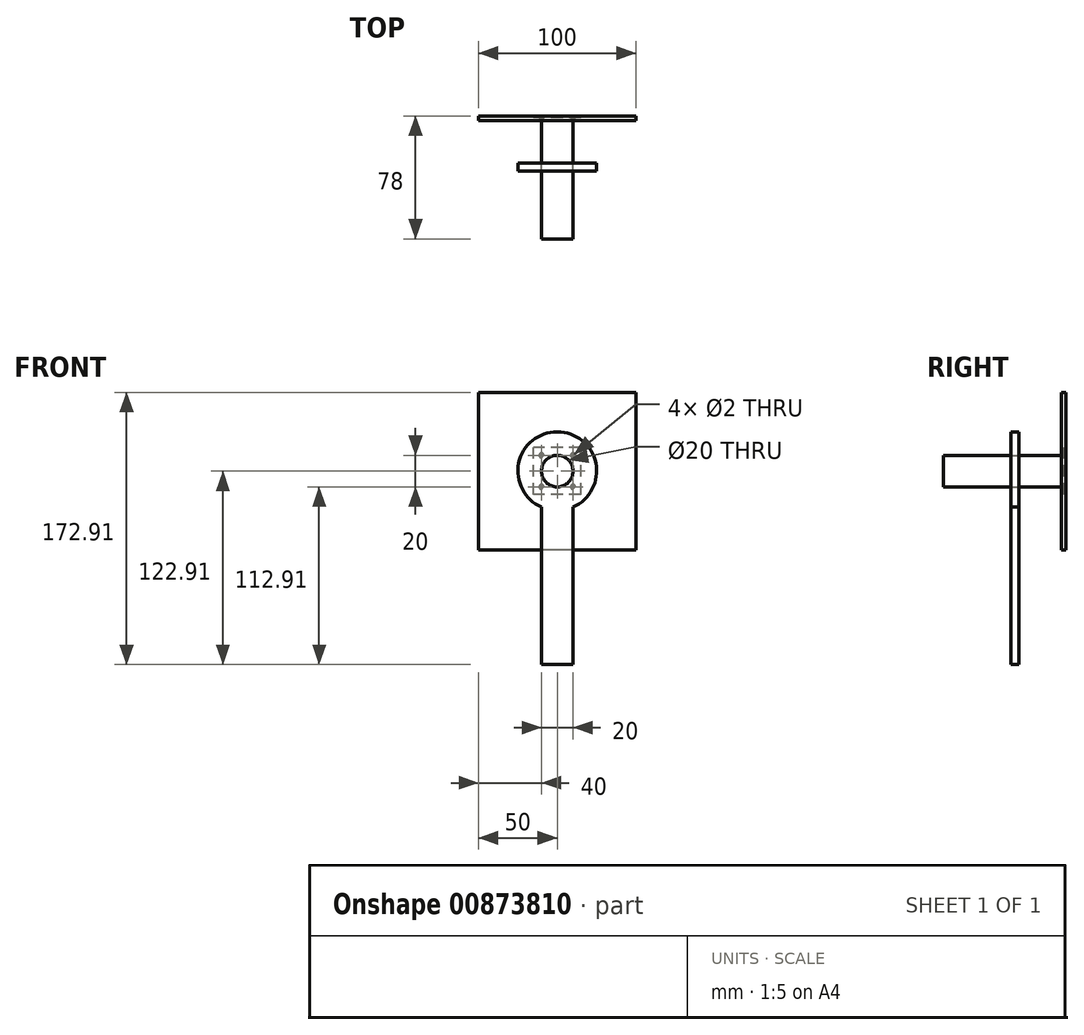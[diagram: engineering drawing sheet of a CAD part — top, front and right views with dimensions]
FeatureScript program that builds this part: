
annotation { "Feature Type Name" : "Feature", "Feature Type Description" : "" }
export const myFeature = defineFeature(function(context is Context, id is Id, definition is map)
    precondition{}
    {
        {
            var Q0;
            Q0=qCreatedBy(makeId("Front.planeOp"),FACE);
            var sketch = newSketch(context, id + "F0", { "sketchPlane" : qUnion([Q0])});
            skArc(sketch, "E0", {"start": v(0, 25) * mm, "mid": v(25, 0) * mm, "end": v(0, -25) * mm});
            skLineSegment(sketch, "E1", {"start": v(0, -25) * mm, "end": v(0, -122.91) * mm});
            skLineSegment(sketch, "E2", {"start": v(0, -122.91) * mm, "end": v(10, -122.91) * mm});
            skLineSegment(sketch, "E3", {"start": v(10, -122.91) * mm, "end": v(10, -22.91) * mm});
            skLineSegment(sketch, "E4", {"start": v(0, 25) * mm, "end": v(0, -25) * mm, "construction": true});
            skArc(sketch, "E5.MirrorCS", {"start": v(0, 25) * mm, "mid": v(-25, 0) * mm, "end": v(0, -25) * mm});
            skLineSegment(sketch, "E6.MirrorCS", {"start": v(-10, -122.91) * mm, "end": v(-10, -22.91) * mm});
            skLineSegment(sketch, "E7", {"start": v(-10, -122.91) * mm, "end": v(0, -122.91) * mm});
            skSolve(sketch);
        }
        {
            var Q0;
            Q0 = qSketchRegion(id + "F0", true);
            extrude(context, id + "F1", {"entities" : qUnion([Q0]), "depth" : 5 * mm, "offsetDistance" : 25 * mm});
        }
        {
            var Q0;
            Q0=qCreatedBy(makeId("Front.planeOp"),FACE);
            var sketch = newSketch(context, id + "F2", { "sketchPlane" : qUnion([Q0])});
            skCircle(sketch, "E8", {"center": v(0, 0) * mm, "radius": 10 * mm});
            skSolve(sketch);
        }
        {
            var Q0;
            Q0 = qSketchRegion(id + "F2", true);
            extrude(context, id + "F3", {"entities" : qUnion([Q0]), "depth" : 75 * mm, "offsetDistance" : 25 * mm});
        }
        {
            var Q0;
            Q0=makeQuery(id+"F3.opExtrude","SWEPT_BODY",BODY,{"disambiguationData":[OSD([sQuery(id+"F2.wireOp",EDGE,"E8")])]});
            var Q1;
            Q1=makeQuery(id+"F1.opExtrude","SWEPT_BODY",BODY,{"disambiguationData":[OSD([sQuery(id+"F0.wireOp",EDGE,"E0"),sQuery(id+"F0.wireOp",EDGE,"E2"),sQuery(id+"F0.wireOp",EDGE,"E3"),sQuery(id+"F0.wireOp",EDGE,"E5.MirrorCS"),sQuery(id+"F0.wireOp",EDGE,"E6.MirrorCS"),sQuery(id+"F0.wireOp",EDGE,"E7")])]});
            booleanBodies(context, id + "F4", {"operationType" : BooleanOperationType.SUBTRACTION, "tools" : qUnion([Q0]), "targets" : qUnion([Q1]), "keepTools" : true});
        }
        {
            var Q0;
            Q0=qCreatedBy(makeId("Front.planeOp"),FACE);
            var sketch = newSketch(context, id + "F5", { "sketchPlane" : qUnion([Q0])});
            skLineSegment(sketch, "E9.bottom", {"start": v(50, -50) * mm, "end": v(-50, -50) * mm});
            skLineSegment(sketch, "E9.top", {"start": v(50, 50) * mm, "end": v(-50, 50) * mm});
            skLineSegment(sketch, "E9.left", {"start": v(50, -50) * mm, "end": v(50, 50) * mm});
            skLineSegment(sketch, "E9.right", {"start": v(-50, -50) * mm, "end": v(-50, 50) * mm});
            skPoint(sketch, "E9.middle", {"position": v(0, 0) * mm});
            skSolve(sketch);
        }
        {
            var Q0;
            Q0 = qSketchRegion(id + "F5", true);
            extrude(context, id + "F6", {"entities" : qUnion([Q0]), "depth" : 3 * mm, "offsetDistance" : 25 * mm});
        }
        {
            var Q0;
            Q0=qCreatedBy(makeId("Front.planeOp"),FACE);
            var sketch = newSketch(context, id + "F7", { "sketchPlane" : qUnion([Q0])});
            skLineSegment(sketch, "E10.bottom", {"start": v(15, -15) * mm, "end": v(-15, -15) * mm});
            skLineSegment(sketch, "E10.top", {"start": v(15, 15) * mm, "end": v(-15, 15) * mm});
            skLineSegment(sketch, "E10.left", {"start": v(15, -15) * mm, "end": v(15, 15) * mm});
            skLineSegment(sketch, "E10.right", {"start": v(-15, -15) * mm, "end": v(-15, 15) * mm});
            skPoint(sketch, "E10.middle", {"position": v(0, 0) * mm});
            skSolve(sketch);
        }
        {
            var Q0;
            Q0 = qSketchRegion(id + "F7", true);
            extrude(context, id + "F8", {"entities" : qUnion([Q0]), "depth" : 1 * mm, "offsetDistance" : 25 * mm});
        }
        {
            var Q0;
            Q0=makeQuery(id+"F3.opExtrude","SWEPT_BODY",BODY,{"disambiguationData":[OSD([sQuery(id+"F2.wireOp",EDGE,"E8")])]});
            transform(context, id + "F9", {"entities" : qUnion([Q0]), "transformType" : TransformType.TRANSLATION_3D, "dx" : 0 * mm, "dy" : -3 * mm, "dz" : 0 * mm, "makeCopy" : false});
        }
        {
            var Q0;
            Q0=makeQuery(id+"F1.opExtrude","SWEPT_BODY",BODY,{"disambiguationData":[OSD([sQuery(id+"F0.wireOp",EDGE,"E0"),sQuery(id+"F0.wireOp",EDGE,"E2"),sQuery(id+"F0.wireOp",EDGE,"E3"),sQuery(id+"F0.wireOp",EDGE,"E5.MirrorCS"),sQuery(id+"F0.wireOp",EDGE,"E6.MirrorCS"),sQuery(id+"F0.wireOp",EDGE,"E7")])]});
            transform(context, id + "F10", {"entities" : qUnion([Q0]), "transformType" : TransformType.TRANSLATION_3D, "dx" : 0 * mm, "dy" : -30 * mm, "dz" : 0 * mm, "makeCopy" : false});
        }
        {
            var Q0;
            Q0=makeQuery(id+"F8.opExtrude","CAP_FACE",FACE,{"disambiguationData":[OSD([sQuery(id+"F7.wireOp",EDGE,"E10.bottom"),sQuery(id+"F7.wireOp",EDGE,"E10.top"),sQuery(id+"F7.wireOp",EDGE,"E10.left"),sQuery(id+"F7.wireOp",EDGE,"E10.right")])],"isStart":false});
            var sketch = newSketch(context, id + "F11", { "sketchPlane" : qUnion([Q0])});
            skPoint(sketch, "E11", {"position": v(-10, 10) * mm});
            skPoint(sketch, "E12.MirrorP", {"position": v(-10, -10) * mm});
            skPoint(sketch, "E13.MirrorP", {"position": v(10, 10) * mm});
            skPoint(sketch, "E14.MirrorP", {"position": v(10, -10) * mm});
            skSolve(sketch);
        }
        {
            var Q0;
            Q0=sQuery(id+"F11.wireOp",VERTEX,"E11");
            var Q1;
            Q1=sQuery(id+"F11.wireOp",VERTEX,"E13.MirrorP");
            var Q2;
            Q2=sQuery(id+"F11.wireOp",VERTEX,"E12.MirrorP");
            var Q3;
            Q3=sQuery(id+"F11.wireOp",VERTEX,"E14.MirrorP");
            var Q4;
            Q4=makeQuery(id+"F3.opExtrude","SWEPT_BODY",BODY,{"disambiguationData":[OSD([sQuery(id+"F2.wireOp",EDGE,"E8")])]});
            var Q5;
            Q5=makeQuery(id+"F6.opExtrude","SWEPT_BODY",BODY,{"disambiguationData":[OSD([sQuery(id+"F5.wireOp",EDGE,"E9.bottom"),sQuery(id+"F5.wireOp",EDGE,"E9.top"),sQuery(id+"F5.wireOp",EDGE,"E9.left"),sQuery(id+"F5.wireOp",EDGE,"E9.right")])]});
            hole(context, id + "F12", {"style" : HoleStyle.C_SINK, "endStyle" : HoleEndStyle.BLIND, "holeDiameter" : 2 * mm, "cSinkDiameter" : 3 * mm, "cSinkAngle" : 90 * degree, "majorDiameter" : 5 * mm, "holeDepth" : 3 * mm, "isTappedThrough" : true, "tappedDepth" : 12 * mm, "tapClearance" : 3, "startFromSketch" : true, "locations" : qUnion([Q0, Q1, Q2, Q3]), "scope" : qUnion([Q4, Q5])});
        }
        {
            var Q0;
            Q0=makeQuery(id+"F8.opExtrude","CAP_FACE",FACE,{"disambiguationData":[OSD([sQuery(id+"F7.wireOp",EDGE,"E10.bottom"),sQuery(id+"F7.wireOp",EDGE,"E10.top"),sQuery(id+"F7.wireOp",EDGE,"E10.left"),sQuery(id+"F7.wireOp",EDGE,"E10.right")])],"isStart":false});
            var sketch = newSketch(context, id + "F13", { "sketchPlane" : qUnion([Q0])});
            skCircle(sketch, "E15.0", {"center": v(-10, -10) * mm, "radius": 1.5 * mm});
            skSolve(sketch);
        }
        {
            var Q0;
            Q0 = qSketchRegion(id + "F13", true);
            var Q1;
            Q1=makeQuery(id+"F6.opExtrude","CAP_FACE",FACE,{"disambiguationData":[OSD([sQuery(id+"F5.wireOp",EDGE,"E9.bottom"),sQuery(id+"F5.wireOp",EDGE,"E9.top"),sQuery(id+"F5.wireOp",EDGE,"E9.left"),sQuery(id+"F5.wireOp",EDGE,"E9.right")])],"isStart":true});
            extrude(context, id + "F14", {"entities" : qUnion([Q0]), "endBound" : BoundingType.UP_TO_SURFACE, "oppositeDirection" : true, "depth" : 25 * mm, "endBoundEntityFace" : qUnion([Q1]), "offsetDistance" : 25 * mm});
        }
        {
            var Q0;
            Q0=makeQuery(id+"F3.opExtrude","SWEPT_BODY",BODY,{"disambiguationData":[OSD([sQuery(id+"F2.wireOp",EDGE,"E8")])]});
            var Q1;
            Q1=makeQuery(id+"F6.opExtrude","SWEPT_BODY",BODY,{"disambiguationData":[OSD([sQuery(id+"F5.wireOp",EDGE,"E9.bottom"),sQuery(id+"F5.wireOp",EDGE,"E9.top"),sQuery(id+"F5.wireOp",EDGE,"E9.left"),sQuery(id+"F5.wireOp",EDGE,"E9.right")])]});
            var Q2;
            Q2=makeQuery(id+"F14.opExtrude","SWEPT_BODY",BODY,{"disambiguationData":[OSD([sQuery(id+"F13.wireOp",EDGE,"E15.0")])]});
            booleanBodies(context, id + "F15", {"operationType" : BooleanOperationType.SUBTRACTION, "tools" : qUnion([Q0, Q1]), "targets" : qUnion([Q2]), "keepTools" : true});
        }
    });
